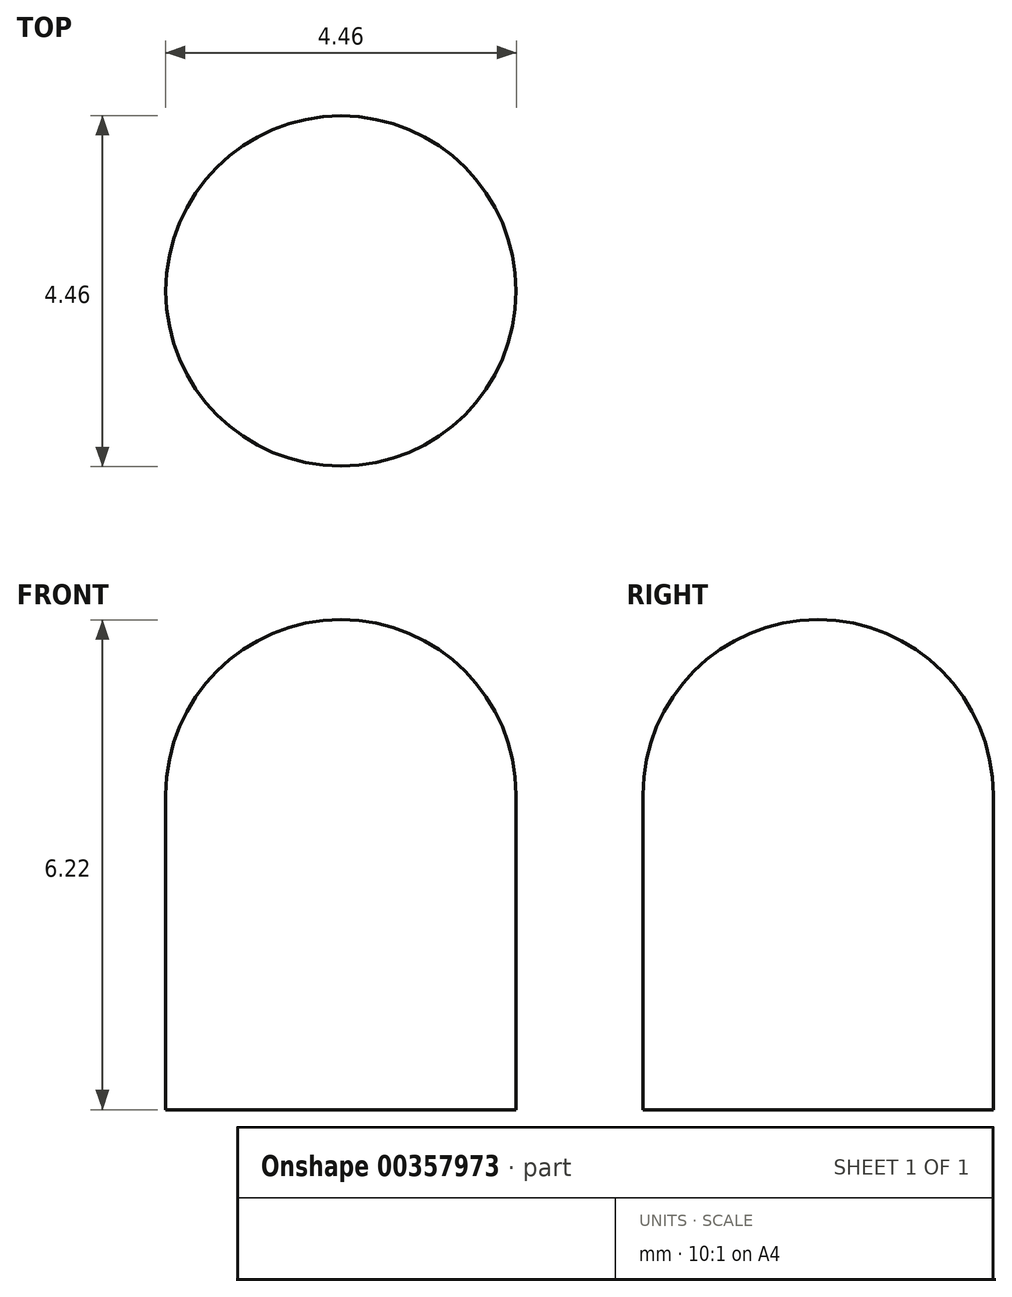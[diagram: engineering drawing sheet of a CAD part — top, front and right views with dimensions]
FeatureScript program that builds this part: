
annotation { "Feature Type Name" : "Feature", "Feature Type Description" : "" }
export const myFeature = defineFeature(function(context is Context, id is Id, definition is map)
    precondition{}
    {
        {
            var Q0;
            Q0=qCreatedBy(makeId("Top.planeOp"),FACE);
            var sketch = newSketch(context, id + "F0", { "sketchPlane" : qUnion([Q0])});
            skCircle(sketch, "E0", {"center": v(0, 0) * mm, "radius": 2.23 * mm});
            skSolve(sketch);
        }
        {
            var Q0;
            Q0 = qSketchRegion(id + "F0", true);
            extrude(context, id + "F1", {"entities" : qUnion([Q0]), "depth" : 4 * mm});
        }
        {
            var Q0;
            Q0=makeQuery(id+"F1.opExtrude","CAP_FACE",FACE,{"disambiguationData":[OSD([sQuery(id+"F0.wireOp",EDGE,"E0")])],"isStart":false});
            var sketch = newSketch(context, id + "F2", { "sketchPlane" : qUnion([Q0])});
            skArc(sketch, "E1", {"start": v(2.23, 0) * mm, "mid": v(0, 2.23) * mm, "end": v(-2.23, 0) * mm});
            skLineSegment(sketch, "E2", {"start": v(-2.23, 0) * mm, "end": v(2.23, 0) * mm});
            skSolve(sketch);
        }
        {
            var Q0;
            Q0 = qSketchRegion(id + "F2", true);
            var Q1;
            Q1=sQuery(id+"F2.wireOp",EDGE,"E2");
            revolve(context, id + "F3", {"operationType" : NewBodyOperationType.ADD, "entities" : qUnion([Q0]), "axis" : qUnion([Q1]), "revolveType" : RevolveType.FULL});
        }
    });
